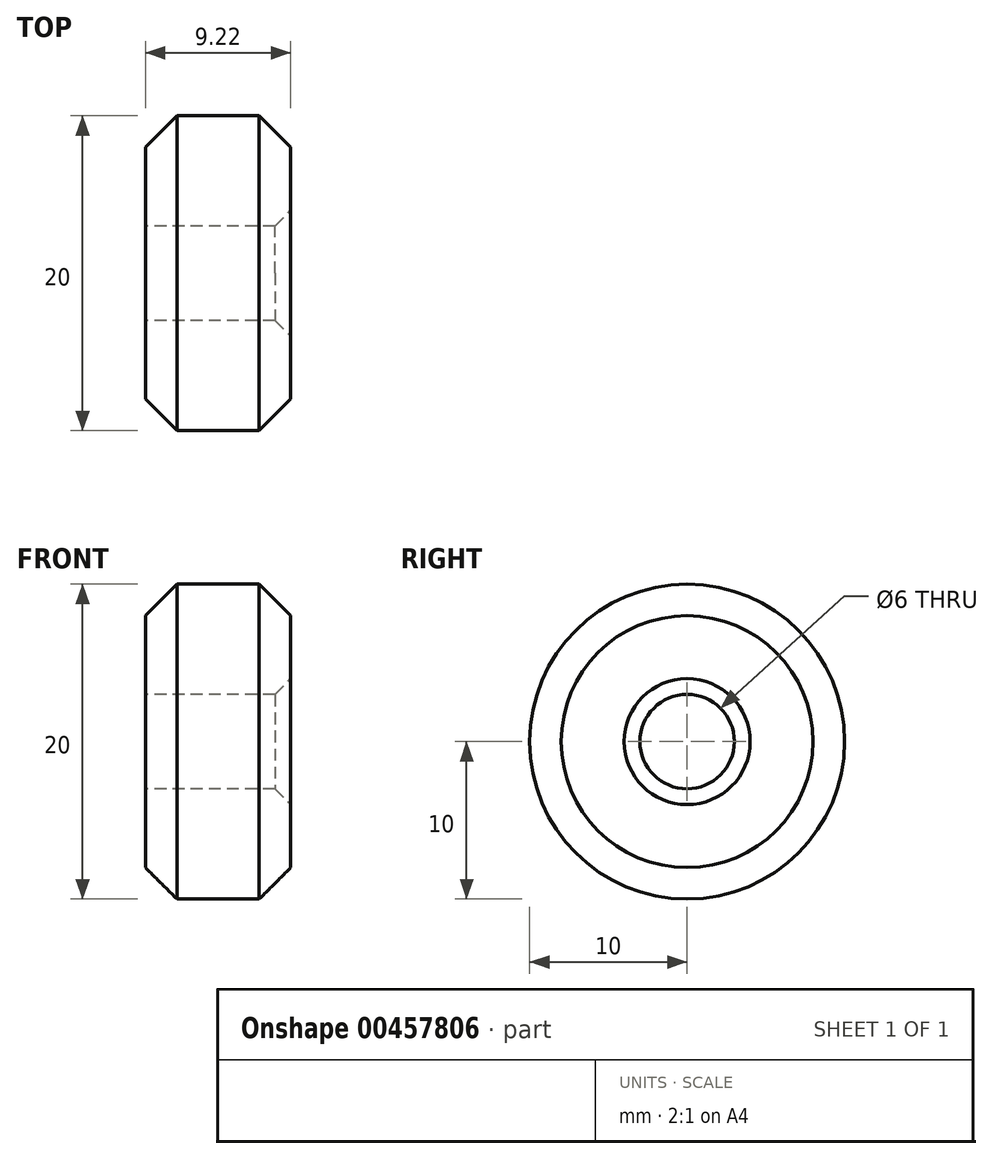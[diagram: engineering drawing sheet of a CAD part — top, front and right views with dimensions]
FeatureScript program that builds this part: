
annotation { "Feature Type Name" : "Feature", "Feature Type Description" : "" }
export const myFeature = defineFeature(function(context is Context, id is Id, definition is map)
    precondition{}
    {
        {
            var Q0;
            Q0=qCreatedBy(makeId("Front.planeOp"),FACE);
            var sketch = newSketch(context, id + "F0", { "sketchPlane" : qUnion([Q0])});
            skLineSegment(sketch, "E0", {"start": v(-8.35, 0) * mm, "end": v(8.72, 0) * mm, "construction": true});
            skLineSegment(sketch, "E1.bottom", {"start": v(4.61, 10) * mm, "end": v(-4.61, 10) * mm});
            skLineSegment(sketch, "E1.left", {"start": v(4.61, 10) * mm, "end": v(4.61, 0) * mm});
            skLineSegment(sketch, "E1.right", {"start": v(-4.61, 10) * mm, "end": v(-4.61, 0) * mm});
            skPoint(sketch, "E1.middle", {"position": v(0, 0) * mm});
            skLineSegment(sketch, "E2", {"start": v(-4.61, 3) * mm, "end": v(4.61, 3) * mm});
            skSolve(sketch);
        }
        {
            var Q0;
            {var subQ0=sQuery(id+"F0.wireOp",EDGE,"E1.bottom");Q0=makeQuery(id+"F0.imprint","IMPRINT",FACE,{"disambiguationData":[TD([[makeQuery(id+"F0.imprint","IMPRINT",EDGE,{"derivedFrom":subQ0}),1.0]])]});}
            var Q1;
            Q1=sQuery(id+"F0.wireOp",EDGE,"E0");
            revolve(context, id + "F1", {"entities" : qUnion([Q0]), "axis" : qUnion([Q1]), "revolveType" : RevolveType.FULL});
        }
        {
            var Q0;
            Q0=makeQuery(id+"F1.opRevolve","SWEPT_EDGE",EDGE,{"disambiguationData":[OSD([sQuery(id+"F0.wireOp",EDGE,"E1.bottom"),sQuery(id+"F0.wireOp",EDGE,"E1.right")])]});
            var Q1;
            Q1=makeQuery(id+"F1.opRevolve","SWEPT_EDGE",EDGE,{"disambiguationData":[OSD([sQuery(id+"F0.wireOp",EDGE,"E1.bottom"),sQuery(id+"F0.wireOp",EDGE,"E1.left")])]});
            chamfer(context, id + "F2", {"entities" : qUnion([Q0, Q1]), "width" : 2 * mm, "tangentPropagation" : true});
        }
        {
            var Q0;
            Q0=makeQuery(id+"F1.opRevolve","SWEPT_EDGE",EDGE,{"disambiguationData":[OSD([sQuery(id+"F0.wireOp",EDGE,"E1.left"),sQuery(id+"F0.wireOp",EDGE,"E2")])]});
            chamfer(context, id + "F3", {"entities" : qUnion([Q0]), "width" : 1 * mm, "tangentPropagation" : true});
        }
    });
